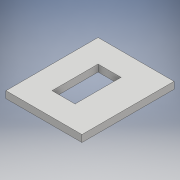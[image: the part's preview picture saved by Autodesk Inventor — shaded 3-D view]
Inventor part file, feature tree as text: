
AUTODESK INVENTOR PART (.ipt)
format: ipt  version: 2017 (Build 210142000, 142)  size: 97,280 bytes
history: native  units: mm
features: extrude x1, sketch x1
ambient origin geometry x8: Origin, YZ Plane, XZ Plane, XY Plane, X Axis, Y Axis, Z Axis, Center Point
bodies: Solid1 (feature_tree)
feature tree (2):
  extrude  "Extrusion1"  [1 undecoded]
  sketch  "Sketch1"  dims[d10=3.0mm d11=0.0mm]
note: 1 required parameter value undecoded (feature->parameter linkage not recoverable at this tier; creation-order binding heuristic only, values carry confidence <= 0.55)
